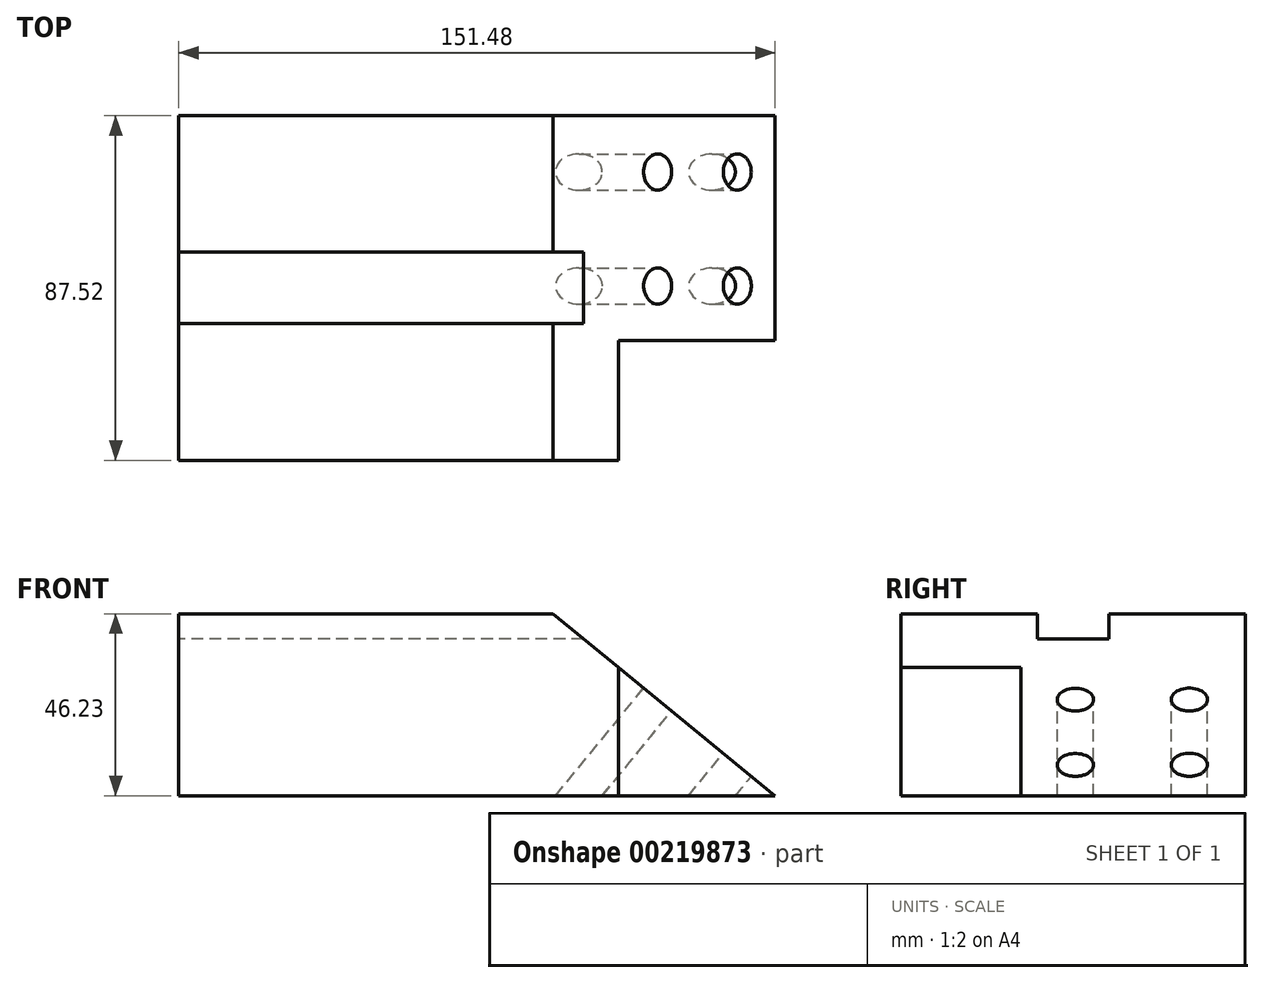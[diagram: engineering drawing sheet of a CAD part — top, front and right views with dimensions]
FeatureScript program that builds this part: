
annotation { "Feature Type Name" : "Feature", "Feature Type Description" : "" }
export const myFeature = defineFeature(function(context is Context, id is Id, definition is map)
    precondition{}
    {
        {
            var Q0;
            Q0=qCreatedBy(makeId("Top.planeOp"),FACE);
            var sketch = newSketch(context, id + "F0", { "sketchPlane" : qUnion([Q0])});
            skLineSegment(sketch, "E0.bottom", {"start": v(75.74, -43.76) * mm, "end": v(-75.74, -43.76) * mm});
            skLineSegment(sketch, "E0.top", {"start": v(75.74, 43.76) * mm, "end": v(-75.74, 43.76) * mm});
            skLineSegment(sketch, "E0.left", {"start": v(75.74, -43.76) * mm, "end": v(75.74, 43.76) * mm});
            skLineSegment(sketch, "E0.right", {"start": v(-75.74, -43.76) * mm, "end": v(-75.74, 43.76) * mm});
            skPoint(sketch, "E0.middle", {"position": v(0, 0) * mm});
            skSolve(sketch);
        }
        {
            var Q0;
            Q0=makeQuery(id+"F0.imprint","IMPRINT",FACE,{"disambiguationData":[TD([[makeQuery(id+"F0.imprint","IMPRINT",EDGE,{"derivedFrom":sQuery(id+"F0.wireOp",EDGE,"E0.bottom")}),-1.0]])]});
            extrude(context, id + "F1", {"entities" : qUnion([Q0]), "depth" : 46.23 * mm});
        }
        {
            var Q0;
            Q0=makeQuery(id+"F1.opExtrude","SWEPT_FACE",FACE,{"disambiguationData":[OSD([sQuery(id+"F0.wireOp",EDGE,"E0.bottom")])]});
            var sketch = newSketch(context, id + "F2", { "sketchPlane" : qUnion([Q0])});
            skLineSegment(sketch, "E1", {"start": v(19.31, 46.23) * mm, "end": v(75.74, 0) * mm});
            skLineSegment(sketch, "E2", {"start": v(75.74, 0) * mm, "end": v(75.74, 46.23) * mm});
            skLineSegment(sketch, "E3", {"start": v(75.74, 46.23) * mm, "end": v(19.31, 46.23) * mm});
            skSolve(sketch);
        }
        {
            var Q0;
            Q0=makeQuery(id+"F2.imprint","IMPRINT",FACE,{"disambiguationData":[TD([[makeQuery(id+"F2.imprint","IMPRINT",EDGE,{"derivedFrom":sQuery(id+"F2.wireOp",EDGE,"E1")}),1.0]])]});
            extrude(context, id + "F3", {"entities" : qUnion([Q0]), "operationType" : NewBodyOperationType.REMOVE, "oppositeDirection" : true, "depth" : 102.87 * mm});
        }
        {
            var Q0;
            Q0=makeQuery(id+"F1.opExtrude","SWEPT_FACE",FACE,{"disambiguationData":[OSD([sQuery(id+"F0.wireOp",EDGE,"E0.bottom")])]});
            var sketch = newSketch(context, id + "F4", { "sketchPlane" : qUnion([Q0])});
            skLineSegment(sketch, "E4", {"start": v(35.97, 32.58) * mm, "end": v(35.97, 0) * mm});
            skLineSegment(sketch, "E5", {"start": v(35.97, 0) * mm, "end": v(75.74, 0) * mm});
            skLineSegment(sketch, "E6", {"start": v(75.74, 0) * mm, "end": v(35.97, 32.58) * mm});
            skSolve(sketch);
        }
        {
            var Q0;
            Q0=makeQuery(id+"F4.imprint","IMPRINT",FACE,{"disambiguationData":[TD([[makeQuery(id+"F4.imprint","IMPRINT",EDGE,{"derivedFrom":sQuery(id+"F4.wireOp",EDGE,"E4")}),1.0]])]});
            extrude(context, id + "F5", {"entities" : qUnion([Q0]), "operationType" : NewBodyOperationType.REMOVE, "oppositeDirection" : true, "depth" : 30.48 * mm});
        }
        {
            var Q0;
            Q0=makeQuery(id+"F1.opExtrude","CAP_FACE",FACE,{"disambiguationData":[OSD([sQuery(id+"F0.wireOp",EDGE,"E0.bottom"),sQuery(id+"F0.wireOp",EDGE,"E0.top"),sQuery(id+"F0.wireOp",EDGE,"E0.left"),sQuery(id+"F0.wireOp",EDGE,"E0.right")])],"isStart":false});
            var sketch = newSketch(context, id + "F6", { "sketchPlane" : qUnion([Q0])});
            skLineSegment(sketch, "E7", {"start": v(28.9, 9.08) * mm, "end": v(-75.74, 9.08) * mm});
            skLineSegment(sketch, "E8", {"start": v(28.9, -9.08) * mm, "end": v(-75.74, -9.08) * mm});
            skLineSegment(sketch, "E9", {"start": v(-75.74, -9.08) * mm, "end": v(-75.74, 9.08) * mm});
            skLineSegment(sketch, "E10", {"start": v(28.9, 9.08) * mm, "end": v(28.9, -9.08) * mm});
            skSolve(sketch);
        }
        {
            var Q0;
            {var subQ0=sQuery(id+"F6.wireOp",EDGE,"E10");Q0=makeQuery(id+"F6.imprint","IMPRINT",FACE,{"disambiguationData":[TD([[makeQuery(id+"F6.imprint","IMPRINT",EDGE,{"derivedFrom":subQ0}),-1.0]])]});}
            var Q1;
            {var subQ0=sQuery(id+"F6.wireOp",EDGE,"E9");Q1=makeQuery(id+"F6.imprint","IMPRINT",FACE,{"disambiguationData":[TD([[makeQuery(id+"F6.imprint","IMPRINT",EDGE,{"derivedFrom":subQ0}),-1.0]])]});}
            extrude(context, id + "F7", {"entities" : qUnion([Q0, Q1]), "operationType" : NewBodyOperationType.REMOVE, "oppositeDirection" : true, "depth" : 6.35 * mm});
        }
        {
            var Q0;
            Q0=makeQuery(id+"F3.boolean.opBoolean","COPY",FACE,{"derivedFrom":makeQuery(id+"F3.opExtrude","SWEPT_FACE",FACE,{"disambiguationData":[OSD([sQuery(id+"F2.wireOp",EDGE,"E1")])]})});
            var sketch = newSketch(context, id + "F8", { "sketchPlane" : qUnion([Q0])});
            skCircle(sketch, "E11", {"center": v(20.03, 29.5) * mm, "radius": 4.6 * mm});
            skCircle(sketch, "E12.0.1.0", {"center": v(20.06, 0.54) * mm, "radius": 4.6 * mm});
            skCircle(sketch, "E12.1.0.0", {"center": v(46.2, 29.5) * mm, "radius": 4.6 * mm});
            skCircle(sketch, "E12.1.1.0", {"center": v(46.22, 0.54) * mm, "radius": 4.6 * mm});
            skLineSegment(sketch, "E12.direction1", {"start": v(20.03, 29.5) * mm, "end": v(46.2, 29.5) * mm, "construction": true});
            skLineSegment(sketch, "E12.direction2", {"start": v(20.03, 29.5) * mm, "end": v(20.06, 0.54) * mm, "construction": true});
            skSolve(sketch);
        }
        {
            var Q0;
            Q0=makeQuery(id+"F8.imprint","IMPRINT",FACE,{"disambiguationData":[TD([[makeQuery(id+"F8.imprint","IMPRINT",EDGE,{"derivedFrom":sQuery(id+"F8.wireOp",EDGE,"E12.0.1.0")}),1.0]])]});
            var Q1;
            Q1=makeQuery(id+"F8.imprint","IMPRINT",FACE,{"disambiguationData":[TD([[makeQuery(id+"F8.imprint","IMPRINT",EDGE,{"derivedFrom":sQuery(id+"F8.wireOp",EDGE,"E11")}),1.0]])]});
            var Q2;
            Q2=makeQuery(id+"F8.imprint","IMPRINT",FACE,{"disambiguationData":[TD([[makeQuery(id+"F8.imprint","IMPRINT",EDGE,{"derivedFrom":sQuery(id+"F8.wireOp",EDGE,"E12.1.0.0")}),1.0]])]});
            var Q3;
            Q3=makeQuery(id+"F8.imprint","IMPRINT",FACE,{"disambiguationData":[TD([[makeQuery(id+"F8.imprint","IMPRINT",EDGE,{"derivedFrom":sQuery(id+"F8.wireOp",EDGE,"E12.1.1.0")}),1.0]])]});
            extrude(context, id + "F9", {"entities" : qUnion([Q0, Q1, Q2, Q3]), "operationType" : NewBodyOperationType.REMOVE, "oppositeDirection" : true, "depth" : 52.32 * mm});
        }
    });
